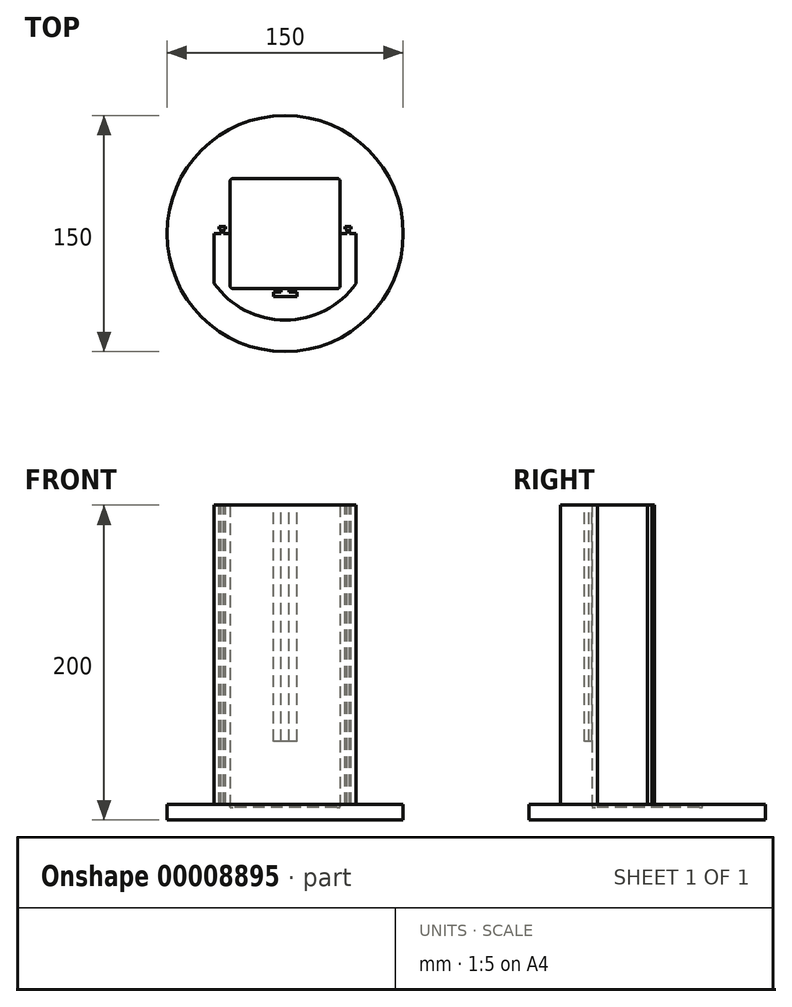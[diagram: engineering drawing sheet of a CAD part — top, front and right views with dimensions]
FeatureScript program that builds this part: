
annotation { "Feature Type Name" : "Feature", "Feature Type Description" : "" }
export const myFeature = defineFeature(function(context is Context, id is Id, definition is map)
    precondition{}
    {
        {
            var Q0;
            Q0=qCreatedBy(makeId("Top.planeOp"),FACE);
            var sketch = newSketch(context, id + "F0", { "sketchPlane" : qUnion([Q0])});
            skCircle(sketch, "E0", {"center": v(0, 0) * mm, "radius": 75 * mm});
            skSolve(sketch);
        }
        {
            var Q0;
            Q0=makeQuery(id+"F0.imprint","IMPRINT",FACE,{"disambiguationData":[TD([[makeQuery(id+"F0.imprint","IMPRINT",EDGE,{"derivedFrom":sQuery(id+"F0.wireOp",EDGE,"E0")}),1.0]])]});
            extrude(context, id + "F1", {"entities" : qUnion([Q0]), "oppositeDirection" : true, "depth" : 10 * mm});
        }
        {
            var Q0;
            Q0=makeQuery(id+"F1.opExtrude","CAP_FACE",FACE,{"disambiguationData":[OSD([sQuery(id+"F0.wireOp",EDGE,"E0")])],"isStart":true});
            var sketch = newSketch(context, id + "F2", { "sketchPlane" : qUnion([Q0])});
            skSolve(sketch);
        }
        {
            var Q0;
            Q0=makeQuery(id+"F2.imprint","IMPRINT",FACE,{"disambiguationData":[TD([[makeQuery(id+"F2.imprint","IMPRINT",EDGE,{"derivedFrom":makeQuery(id+"F1.opExtrude","CAP_EDGE",EDGE,{"disambiguationData":[OSD([sQuery(id+"F0.wireOp",EDGE,"E0")])],"isStart":true})}),1.0]])]});
            var sketch = newSketch(context, id + "F3", { "sketchPlane" : qUnion([Q0])});
            skLineSegment(sketch, "E1", {"start": v(55, 0) * mm, "end": v(-55, 0) * mm});
            skLineSegment(sketch, "E2", {"start": v(0, 0) * mm, "end": v(0, -35) * mm});
            skLineSegment(sketch, "E3", {"start": v(33, -35) * mm, "end": v(-33, -35) * mm});
            skLineSegment(sketch, "E4.0", {"start": v(-35, 0) * mm, "end": v(-35, -33) * mm});
            skLineSegment(sketch, "E5.0", {"start": v(35, 0) * mm, "end": v(35, -33) * mm});
            skArc(sketch, "E6.filletArc", {"start": v(-35, -33) * mm, "mid": v(-34.41, -34.41) * mm, "end": v(-33, -35) * mm});
            skArc(sketch, "E7.filletArc", {"start": v(33, -35) * mm, "mid": v(34.41, -34.41) * mm, "end": v(35, -33) * mm});
            skLineSegment(sketch, "E8.0", {"start": v(-45, 0) * mm, "end": v(-45, -31.62) * mm});
            skLineSegment(sketch, "E9.0", {"start": v(45, 0) * mm, "end": v(45, -31.62) * mm});
            skLineSegment(sketch, "E10.0.MirrorCS", {"start": v(35, 0) * mm, "end": v(35, 33) * mm});
            skLineSegment(sketch, "E11.0.MirrorCS", {"start": v(0, 0) * mm, "end": v(0, 35) * mm});
            skLineSegment(sketch, "E12.0.MirrorCS", {"start": v(-35, 0) * mm, "end": v(-35, 33) * mm});
            skArc(sketch, "E13.0.MirrorCS", {"start": v(-35, 33) * mm, "mid": v(-34.41, 34.41) * mm, "end": v(-33, 35) * mm});
            skArc(sketch, "E14.0.MirrorCS", {"start": v(33, 35) * mm, "mid": v(34.41, 34.41) * mm, "end": v(35, 33) * mm});
            skLineSegment(sketch, "E15.0.MirrorCS", {"start": v(33, 35) * mm, "end": v(-33, 35) * mm});
            skCircle(sketch, "E16.0", {"center": v(0, 0) * mm, "radius": 55 * mm});
            skSolve(sketch);
        }
        {
            var Q0;
            {var subQ5=sQuery(id+"F3.wireOp",EDGE,"E4.0");Q0=makeQuery(id+"F3.imprint","IMPRINT",FACE,{"disambiguationData":[TD([[makeQuery(id+"F3.imprint","IMPRINT",EDGE,{"derivedFrom":subQ5}),-1.0]])]});}
            extrude(context, id + "F4", {"entities" : qUnion([Q0]), "operationType" : NewBodyOperationType.ADD, "depth" : 190 * mm});
        }
        {
            var Q0;
            Q0=makeQuery(id+"F4.opExtrude","CAP_FACE",FACE,{"disambiguationData":[OSD([sQuery(id+"F3.wireOp",EDGE,"E1"),sQuery(id+"F3.wireOp",EDGE,"E3"),sQuery(id+"F3.wireOp",EDGE,"E4.0"),sQuery(id+"F3.wireOp",EDGE,"E5.0"),sQuery(id+"F3.wireOp",EDGE,"E6.filletArc"),sQuery(id+"F3.wireOp",EDGE,"E7.filletArc"),sQuery(id+"F3.wireOp",EDGE,"E8.0"),sQuery(id+"F3.wireOp",EDGE,"E9.0"),sQuery(id+"F3.wireOp",EDGE,"30718d8a-f85b-44eb-b5a2-9b228f8a43ee.trimOffspring")])],"isStart":false});
            var sketch = newSketch(context, id + "F5", { "sketchPlane" : qUnion([Q0])});
            skLineSegment(sketch, "E17", {"start": v(-45, 0) * mm, "end": v(-45, 5) * mm});
            skLineSegment(sketch, "E18", {"start": v(45, 0) * mm, "end": v(45, 5) * mm});
            skLineSegment(sketch, "E19.0", {"start": v(-37.5, 2.5) * mm, "end": v(-37.5, 5) * mm});
            skLineSegment(sketch, "E20.0", {"start": v(-38.75, 0) * mm, "end": v(-38.75, 2.5) * mm});
            skLineSegment(sketch, "E21.0", {"start": v(-42.5, 2.5) * mm, "end": v(-42.5, 5) * mm});
            skLineSegment(sketch, "E22.0", {"start": v(-41.25, 0) * mm, "end": v(-41.25, 2.5) * mm});
            skLineSegment(sketch, "E23.0", {"start": v(42.5, 2.5) * mm, "end": v(42.5, 5) * mm});
            skLineSegment(sketch, "E24.0", {"start": v(37.5, 2.5) * mm, "end": v(37.5, 5) * mm});
            skLineSegment(sketch, "E25.0", {"start": v(41.25, 0) * mm, "end": v(41.25, 2.5) * mm});
            skLineSegment(sketch, "E26.0", {"start": v(38.75, 0) * mm, "end": v(38.75, 2.5) * mm});
            skLineSegment(sketch, "E27", {"start": v(42.5, 5) * mm, "end": v(37.5, 5) * mm});
            skLineSegment(sketch, "E28", {"start": v(-42.5, 5) * mm, "end": v(-37.5, 5) * mm});
            skLineSegment(sketch, "E29.0", {"start": v(-42.5, 2.5) * mm, "end": v(-41.25, 2.5) * mm});
            skLineSegment(sketch, "E30.trimOffspring", {"start": v(-38.75, 2.5) * mm, "end": v(-37.5, 2.5) * mm});
            skLineSegment(sketch, "E31.0", {"start": v(42.5, 2.5) * mm, "end": v(41.25, 2.5) * mm});
            skLineSegment(sketch, "E32.trimOffspring", {"start": v(38.75, 2.5) * mm, "end": v(37.5, 2.5) * mm});
            skLineSegment(sketch, "E33.0", {"start": v(-42.5, 4.5) * mm, "end": v(-37.5, 4.5) * mm});
            skLineSegment(sketch, "E34.0", {"start": v(-42, 2.5) * mm, "end": v(-42, 5) * mm});
            skLineSegment(sketch, "E35.0", {"start": v(-38, 2.5) * mm, "end": v(-38, 5) * mm});
            skLineSegment(sketch, "E36.0", {"start": v(-42.5, 3) * mm, "end": v(-40.75, 3) * mm});
            skLineSegment(sketch, "E37.0", {"start": v(-39.25, 3) * mm, "end": v(-37.5, 3) * mm});
            skLineSegment(sketch, "E38.0", {"start": v(-40.75, 0) * mm, "end": v(-40.75, 3) * mm});
            skLineSegment(sketch, "E39.0", {"start": v(-39.25, 0) * mm, "end": v(-39.25, 3) * mm});
            skLineSegment(sketch, "E40.0", {"start": v(42.5, 4.5) * mm, "end": v(37.5, 4.5) * mm});
            skLineSegment(sketch, "E41.0", {"start": v(38, 2.5) * mm, "end": v(38, 5) * mm});
            skLineSegment(sketch, "E42.0", {"start": v(42, 2.5) * mm, "end": v(42, 5) * mm});
            skLineSegment(sketch, "E43.0", {"start": v(42.5, 3) * mm, "end": v(40.75, 3) * mm});
            skLineSegment(sketch, "E44.0", {"start": v(39.25, 3) * mm, "end": v(37.5, 3) * mm});
            skLineSegment(sketch, "E45.0", {"start": v(39.25, 0) * mm, "end": v(39.25, 3) * mm});
            skLineSegment(sketch, "E46.0", {"start": v(40.75, 0) * mm, "end": v(40.75, 3) * mm});
            skSolve(sketch);
        }
        {
            var Q0;
            {var subQ1=sQuery(id+"F5.wireOp",EDGE,"E45.0");Q0=makeQuery(id+"F5.imprint","IMPRINT",FACE,{"disambiguationData":[TD([[makeQuery(id+"F5.imprint","IMPRINT",EDGE,{"derivedFrom":subQ1}),-1.0]])]});}
            var Q1;
            {var subQ3=sQuery(id+"F5.wireOp",EDGE,"E38.0");Q1=makeQuery(id+"F5.imprint","IMPRINT",FACE,{"disambiguationData":[TD([[makeQuery(id+"F5.imprint","IMPRINT",EDGE,{"derivedFrom":subQ3}),-1.0]])]});}
            extrude(context, id + "F6", {"entities" : qUnion([Q0, Q1]), "operationType" : NewBodyOperationType.ADD, "oppositeDirection" : true, "depth" : 200 * mm});
        }
        {
            var Q0;
            {var subQ0=sQuery(id+"F3.wireOp",EDGE,"E1");Q0=makeQuery(id+"F6.boolean.opBoolean","MERGE",FACE,{"derivedFrom":[makeQuery(id+"F4.opExtrude","CAP_FACE",FACE,{"disambiguationData":[OSD([subQ0,sQuery(id+"F3.wireOp",EDGE,"E3"),sQuery(id+"F3.wireOp",EDGE,"E4.0"),sQuery(id+"F3.wireOp",EDGE,"E5.0"),sQuery(id+"F3.wireOp",EDGE,"E6.filletArc"),sQuery(id+"F3.wireOp",EDGE,"E7.filletArc"),sQuery(id+"F3.wireOp",EDGE,"E8.0"),sQuery(id+"F3.wireOp",EDGE,"E9.0"),sQuery(id+"F3.wireOp",EDGE,"30718d8a-f85b-44eb-b5a2-9b228f8a43ee.trimOffspring")])],"isStart":false}),makeQuery(id+"F6.opExtrude","CAP_FACE",FACE,{"disambiguationData":[OSD([subQ0,sQuery(id+"F5.wireOp",EDGE,"E33.0"),sQuery(id+"F5.wireOp",EDGE,"E34.0"),sQuery(id+"F5.wireOp",EDGE,"E35.0"),sQuery(id+"F5.wireOp",EDGE,"E36.0"),sQuery(id+"F5.wireOp",EDGE,"E37.0"),sQuery(id+"F5.wireOp",EDGE,"E38.0"),sQuery(id+"F5.wireOp",EDGE,"E39.0")])],"isStart":true}),makeQuery(id+"F6.opExtrude","CAP_FACE",FACE,{"disambiguationData":[OSD([subQ0,sQuery(id+"F5.wireOp",EDGE,"E40.0"),sQuery(id+"F5.wireOp",EDGE,"E41.0"),sQuery(id+"F5.wireOp",EDGE,"E42.0"),sQuery(id+"F5.wireOp",EDGE,"E43.0"),sQuery(id+"F5.wireOp",EDGE,"E44.0"),sQuery(id+"F5.wireOp",EDGE,"E45.0"),sQuery(id+"F5.wireOp",EDGE,"E46.0")])],"isStart":true})]});}
            var sketch = newSketch(context, id + "F7", { "sketchPlane" : qUnion([Q0])});
            skLineSegment(sketch, "E47", {"start": v(-35, -33) * mm, "end": v(-35, -42.04) * mm});
            skLineSegment(sketch, "E48", {"start": v(35, -33) * mm, "end": v(35, -41.78) * mm});
            skLineSegment(sketch, "E49", {"start": v(-33, -35) * mm, "end": v(33, -35) * mm});
            skLineSegment(sketch, "E50.0", {"start": v(-2.5, -35) * mm, "end": v(-2.5, -37) * mm});
            skLineSegment(sketch, "E51.0", {"start": v(2.5, -35) * mm, "end": v(2.5, -37) * mm});
            skPoint(sketch, "E52.0.end.orphan", {"position": v(0, -40) * mm});
            skLineSegment(sketch, "E53.0", {"start": v(-7.5, -37) * mm, "end": v(-7.5, -40) * mm});
            skLineSegment(sketch, "E54.0", {"start": v(7.5, -37) * mm, "end": v(7.5, -40) * mm});
            skPoint(sketch, "E55.start.orphan", {"position": v(0, -35) * mm});
            skLineSegment(sketch, "E56", {"start": v(-2.5, -35) * mm, "end": v(-7.5, -35) * mm});
            skLineSegment(sketch, "E57", {"start": v(7.5, -35) * mm, "end": v(2.5, -35) * mm});
            skLineSegment(sketch, "E58.0", {"start": v(7.5, -37) * mm, "end": v(2.5, -37) * mm});
            skLineSegment(sketch, "E59.trimOffspring", {"start": v(-2.5, -37) * mm, "end": v(-7.5, -37) * mm});
            skLineSegment(sketch, "E60.0", {"start": v(-2.5, -40) * mm, "end": v(-7.5, -40) * mm});
            skLineSegment(sketch, "E61.0", {"start": v(7.5, -40) * mm, "end": v(2.5, -40) * mm});
            skLineSegment(sketch, "E62", {"start": v(-2.5, -40) * mm, "end": v(2.5, -40) * mm});
            skSolve(sketch);
        }
        {
            var Q0;
            {var subQ1=sQuery(id+"F7.wireOp",EDGE,"E50.0");Q0=makeQuery(id+"F7.imprint","IMPRINT",FACE,{"disambiguationData":[TD([[makeQuery(id+"F7.imprint","IMPRINT",EDGE,{"derivedFrom":subQ1}),1.0]])]});}
            extrude(context, id + "F8", {"entities" : qUnion([Q0]), "operationType" : NewBodyOperationType.REMOVE, "oppositeDirection" : true, "depth" : 150 * mm});
        }
        {
            var Q0;
            {var subQ3=sQuery(id+"F3.wireOp",EDGE,"E2");Q0=makeQuery(id+"F3.imprint","IMPRINT",FACE,{"disambiguationData":[TD([[makeQuery(id+"F3.imprint","IMPRINT",EDGE,{"derivedFrom":subQ3}),1.0]])]});}
            var Q1;
            {var subQ3=sQuery(id+"F3.wireOp",EDGE,"E2");Q1=makeQuery(id+"F3.imprint","IMPRINT",FACE,{"disambiguationData":[TD([[makeQuery(id+"F3.imprint","IMPRINT",EDGE,{"derivedFrom":subQ3}),-1.0]])]});}
            var Q2;
            {var subQ2=sQuery(id+"F3.wireOp",EDGE,"E11.0.MirrorCS");Q2=makeQuery(id+"F3.imprint","IMPRINT",FACE,{"disambiguationData":[TD([[makeQuery(id+"F3.imprint","IMPRINT",EDGE,{"derivedFrom":subQ2}),1.0]])]});}
            var Q3;
            {var subQ3=sQuery(id+"F3.wireOp",EDGE,"E10.0.MirrorCS");Q3=makeQuery(id+"F3.imprint","IMPRINT",FACE,{"disambiguationData":[TD([[makeQuery(id+"F3.imprint","IMPRINT",EDGE,{"derivedFrom":subQ3}),1.0]])]});}
            extrude(context, id + "F9", {"entities" : qUnion([Q0, Q1, Q2, Q3]), "operationType" : NewBodyOperationType.REMOVE, "oppositeDirection" : true, "depth" : 2 * mm});
        }
    });
